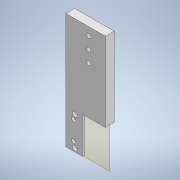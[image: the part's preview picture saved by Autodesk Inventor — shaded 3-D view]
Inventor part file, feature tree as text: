
AUTODESK INVENTOR PART (.ipt)
format: ipt  version: 2022 (Build 260153000, 153)  size: 154,624 bytes
history: native  units: in
note: dims shown in document units (in); Inventor stores cm internally (conversion verified against a paired STEP export)
features: reference x6, extrude x4, sketch x4, other x4, plane x1, projected_geometry x1
ambient origin geometry x8: Origin, YZ Plane, XZ Plane, XY Plane, X Axis, Y Axis, Z Axis, Center Point
bodies: Solid1 (feature_tree)
feature tree (20):
  plane  "Work Plane1"
  extrude  "Extrusion1"  Depth=0.1181in
  extrude  "Extrusion2"  Depth=3.937in TaperAngle=0.0deg
  extrude  "Extrusion4"  Depth=0.3937in
  extrude  "Extrusion5"  Depth=0.9843in
  sketch  "Sketch1"  dims[d0=0.1181in d1=0.0in d3=0.0039in]
  reference  "Reference1"
  reference  "Reference2"
  sketch  "Sketch3"  dims[d4=0.0039in d5=3.937in d6=0.0in]
  reference  "Reference4"
  projected_geometry  "Projected Loop2"
  sketch  "Sketch5"  dims[d17=0.1969in d18=1.5748in d20=0.7874in d21=0.3937in d23=0.3937in]
  sketch  "Sketch6"  dims[d25=0.9843in d26=0.0in d27=0.1969in d28=0.1969in d29=0.1969in d30=0.0in d31=0.0in]
  reference  "Reference7"
  reference  "Reference8"
  reference  "Reference9"
  other  "Linear Rail Assembly.iam"
  other  "Linear Rail End Cap:1"
  other  "Linear Rail Base:1"
  other  "Linear Rail Frame Bracket:1"
